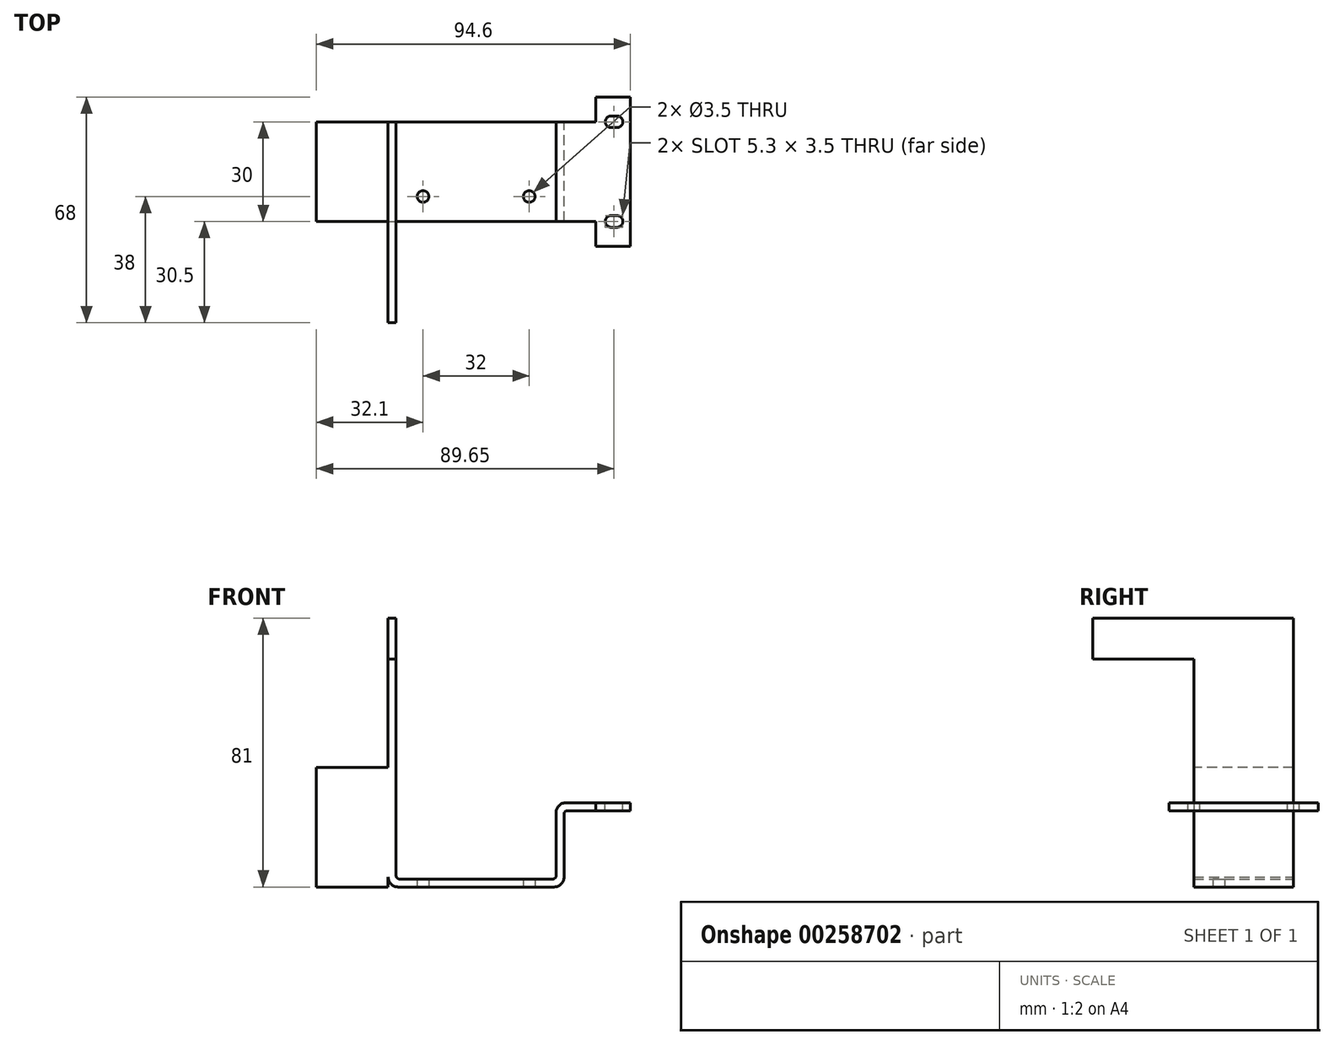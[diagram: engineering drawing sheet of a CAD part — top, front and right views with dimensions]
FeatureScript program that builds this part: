
annotation { "Feature Type Name" : "Feature", "Feature Type Description" : "" }
export const myFeature = defineFeature(function(context is Context, id is Id, definition is map)
    precondition{}
    {
        {
            var Q0;
            Q0=qCreatedBy(makeId("Front.planeOp"),FACE);
            var sketch = newSketch(context, id + "F0", { "sketchPlane" : qUnion([Q0])});
            skLineSegment(sketch, "E0", {"start": v(0, 0) * mm, "end": v(-53, 0) * mm});
            skLineSegment(sketch, "E1", {"start": v(-53, 0) * mm, "end": v(-53, 81) * mm});
            skLineSegment(sketch, "E2", {"start": v(-53, 81) * mm, "end": v(-50.6, 81) * mm});
            skLineSegment(sketch, "E3", {"start": v(-50.6, 81) * mm, "end": v(-50.6, 2.4) * mm});
            skLineSegment(sketch, "E4", {"start": v(-50.6, 2.4) * mm, "end": v(-2.4, 2.4) * mm});
            skLineSegment(sketch, "E5", {"start": v(-2.4, 2.4) * mm, "end": v(-2.4, 25.4) * mm});
            skLineSegment(sketch, "E6", {"start": v(-2.4, 25.4) * mm, "end": v(20, 25.4) * mm});
            skLineSegment(sketch, "E7", {"start": v(20, 25.4) * mm, "end": v(20, 23) * mm});
            skLineSegment(sketch, "E8", {"start": v(20, 23) * mm, "end": v(0, 23) * mm});
            skLineSegment(sketch, "E9", {"start": v(0, 23) * mm, "end": v(0, 0) * mm});
            skSolve(sketch);
        }
        {
            var Q0;
            Q0=makeQuery(id+"F0.imprint","IMPRINT",FACE,{"disambiguationData":[TD([[makeQuery(id+"F0.imprint","IMPRINT",EDGE,{"derivedFrom":sQuery(id+"F0.wireOp",EDGE,"E0")}),-1.0]])]});
            extrude(context, id + "F1", {"entities" : qUnion([Q0]), "endBound" : BoundingType.SYMMETRIC, "depth" : 30 * mm});
        }
        {
            var Q0;
            Q0=makeQuery(id+"F1.opExtrude","CAP_FACE",FACE,{"disambiguationData":[OSD([sQuery(id+"F0.wireOp",EDGE,"E0"),sQuery(id+"F0.wireOp",EDGE,"E1"),sQuery(id+"F0.wireOp",EDGE,"E2"),sQuery(id+"F0.wireOp",EDGE,"E3"),sQuery(id+"F0.wireOp",EDGE,"E4"),sQuery(id+"F0.wireOp",EDGE,"E5"),sQuery(id+"F0.wireOp",EDGE,"E6"),sQuery(id+"F0.wireOp",EDGE,"E7"),sQuery(id+"F0.wireOp",EDGE,"E8"),sQuery(id+"F0.wireOp",EDGE,"E9")])],"isStart":false});
            var sketch = newSketch(context, id + "F2", { "sketchPlane" : qUnion([Q0])});
            skLineSegment(sketch, "E10", {"start": v(-53, 68.7) * mm, "end": v(-50.6, 68.7) * mm});
            skLineSegment(sketch, "E11", {"start": v(9.5, 25.4) * mm, "end": v(9.5, 23) * mm});
            skSolve(sketch);
        }
        {
            var Q0;
            {var subQ0=sQuery(id+"F2.wireOp",EDGE,"E10");Q0=makeQuery(id+"F2.imprint","IMPRINT",FACE,{"disambiguationData":[TD([[makeQuery(id+"F2.imprint","IMPRINT",EDGE,{"derivedFrom":subQ0}),1.0]])]});}
            extrude(context, id + "F3", {"entities" : qUnion([Q0]), "operationType" : NewBodyOperationType.ADD, "depth" : 30.5 * mm});
        }
        {
            var Q0;
            {var subQ0=sQuery(id+"F2.wireOp",EDGE,"E11");Q0=makeQuery(id+"F2.imprint","IMPRINT",FACE,{"disambiguationData":[TD([[makeQuery(id+"F2.imprint","IMPRINT",EDGE,{"derivedFrom":subQ0}),1.0]])]});}
            extrude(context, id + "F4", {"entities" : qUnion([Q0]), "operationType" : NewBodyOperationType.ADD, "depth" : 7.5 * mm});
        }
        {
            var Q0;
            Q0=makeQuery(id+"F1.opExtrude","CAP_FACE",FACE,{"disambiguationData":[OSD([sQuery(id+"F0.wireOp",EDGE,"E0"),sQuery(id+"F0.wireOp",EDGE,"E1"),sQuery(id+"F0.wireOp",EDGE,"E2"),sQuery(id+"F0.wireOp",EDGE,"E3"),sQuery(id+"F0.wireOp",EDGE,"E4"),sQuery(id+"F0.wireOp",EDGE,"E5"),sQuery(id+"F0.wireOp",EDGE,"E6"),sQuery(id+"F0.wireOp",EDGE,"E7"),sQuery(id+"F0.wireOp",EDGE,"E8"),sQuery(id+"F0.wireOp",EDGE,"E9")])],"isStart":true});
            var sketch = newSketch(context, id + "F5", { "sketchPlane" : qUnion([Q0])});
            skLineSegment(sketch, "E12", {"start": v(-9.5, 25.4) * mm, "end": v(-9.5, 23) * mm});
            skSolve(sketch);
        }
        {
            var Q0;
            {var subQ0=sQuery(id+"F5.wireOp",EDGE,"E12");Q0=makeQuery(id+"F5.imprint","IMPRINT",FACE,{"disambiguationData":[TD([[makeQuery(id+"F5.imprint","IMPRINT",EDGE,{"derivedFrom":subQ0}),-1.0]])]});}
            extrude(context, id + "F6", {"entities" : qUnion([Q0]), "operationType" : NewBodyOperationType.ADD, "depth" : 7.5 * mm});
        }
        {
            var Q0;
            {var subQ0=sQuery(id+"F0.wireOp",EDGE,"E6");Q0=makeQuery(id+"F6.boolean.opBoolean","MERGE",FACE,{"derivedFrom":[makeQuery(id+"F4.boolean.opBoolean","MERGE",FACE,{"derivedFrom":[makeQuery(id+"F1.opExtrude","SWEPT_FACE",FACE,{"disambiguationData":[OSD([subQ0])]}),makeQuery(id+"F4.opExtrude","SWEPT_FACE",FACE,{"disambiguationData":[OSD([subQ0])]})]}),makeQuery(id+"F6.opExtrude","SWEPT_FACE",FACE,{"disambiguationData":[OSD([subQ0])]})]});}
            var sketch = newSketch(context, id + "F7", { "sketchPlane" : qUnion([Q0])});
            skCircle(sketch, "E13", {"center": v(14.15, 15) * mm, "radius": 1.75 * mm});
            skCircle(sketch, "E14", {"center": v(15.95, 15) * mm, "radius": 1.75 * mm});
            skCircle(sketch, "E15", {"center": v(14.15, -15) * mm, "radius": 1.75 * mm});
            skCircle(sketch, "E16", {"center": v(15.95, -15) * mm, "radius": 1.75 * mm});
            skLineSegment(sketch, "E17", {"start": v(20, 0) * mm, "end": v(0, 0) * mm, "construction": true});
            skLineSegment(sketch, "E18", {"start": v(14.15, 16.75) * mm, "end": v(15.95, 16.75) * mm});
            skLineSegment(sketch, "E19", {"start": v(15.95, 13.25) * mm, "end": v(14.15, 13.25) * mm});
            skLineSegment(sketch, "E20", {"start": v(14.15, -13.25) * mm, "end": v(15.95, -13.25) * mm});
            skLineSegment(sketch, "E21", {"start": v(14.15, -16.75) * mm, "end": v(15.95, -16.75) * mm});
            skSolve(sketch);
        }
        {
            var Q0;
            {var subQ0=sQuery(id+"F7.wireOp",EDGE,"E15");var subQ1=makeQuery(id+"F7.imprint","INTERSECT",VERTEX,{"derivedFrom":[subQ0,sQuery(id+"F7.wireOp",EDGE,"E20")]});Q0=makeQuery(id+"F7.imprint","IMPRINT",FACE,{"disambiguationData":[TD([[makeQuery(id+"F7.imprint","IMPRINT",EDGE,{"disambiguationData":[TD([[subQ1,1.0]])],"derivedFrom":subQ0}),1.0]])]});}
            var Q1;
            {var subQ0=sQuery(id+"F7.wireOp",EDGE,"E16");var subQ1=sQuery(id+"F7.wireOp",EDGE,"E15");var subQ2=makeQuery(id+"F7.imprint","INTERSECT",VERTEX,{"disambiguationData":[OD(0.0)],"derivedFrom":[subQ1,subQ0]});Q1=makeQuery(id+"F7.imprint","IMPRINT",FACE,{"disambiguationData":[TD([[makeQuery(id+"F7.imprint","IMPRINT",EDGE,{"disambiguationData":[TD([[subQ2,1.0]])],"derivedFrom":subQ1}),1.0]])]});}
            var Q2;
            {var subQ0=sQuery(id+"F7.wireOp",EDGE,"E16");var subQ1=sQuery(id+"F7.wireOp",EDGE,"E15");var subQ2=makeQuery(id+"F7.imprint","INTERSECT",VERTEX,{"disambiguationData":[OD(0.0)],"derivedFrom":[subQ1,subQ0]});Q2=makeQuery(id+"F7.imprint","IMPRINT",FACE,{"disambiguationData":[TD([[makeQuery(id+"F7.imprint","IMPRINT",EDGE,{"disambiguationData":[TD([[subQ2,1.0]])],"derivedFrom":subQ1}),-1.0]])]});}
            var Q3;
            {var subQ0=sQuery(id+"F7.wireOp",EDGE,"E20");Q3=makeQuery(id+"F7.imprint","IMPRINT",FACE,{"disambiguationData":[TD([[makeQuery(id+"F7.imprint","IMPRINT",EDGE,{"derivedFrom":subQ0}),-1.0]])]});}
            var Q4;
            {var subQ0=sQuery(id+"F7.wireOp",EDGE,"E21");Q4=makeQuery(id+"F7.imprint","IMPRINT",FACE,{"disambiguationData":[TD([[makeQuery(id+"F7.imprint","IMPRINT",EDGE,{"derivedFrom":subQ0}),1.0]])]});}
            var Q5;
            {var subQ0=sQuery(id+"F7.wireOp",EDGE,"E13");var subQ1=makeQuery(id+"F7.imprint","INTERSECT",VERTEX,{"derivedFrom":[subQ0,sQuery(id+"F7.wireOp",EDGE,"E18")]});Q5=makeQuery(id+"F7.imprint","IMPRINT",FACE,{"disambiguationData":[TD([[makeQuery(id+"F7.imprint","IMPRINT",EDGE,{"disambiguationData":[TD([[subQ1,1.0]])],"derivedFrom":subQ0}),1.0]])]});}
            var Q6;
            {var subQ0=sQuery(id+"F7.wireOp",EDGE,"E14");var subQ1=sQuery(id+"F7.wireOp",EDGE,"E13");var subQ2=makeQuery(id+"F7.imprint","INTERSECT",VERTEX,{"disambiguationData":[OD(0.0)],"derivedFrom":[subQ1,subQ0]});Q6=makeQuery(id+"F7.imprint","IMPRINT",FACE,{"disambiguationData":[TD([[makeQuery(id+"F7.imprint","IMPRINT",EDGE,{"disambiguationData":[TD([[subQ2,1.0]])],"derivedFrom":subQ1}),1.0]])]});}
            var Q7;
            {var subQ0=sQuery(id+"F7.wireOp",EDGE,"E14");var subQ1=sQuery(id+"F7.wireOp",EDGE,"E13");var subQ2=makeQuery(id+"F7.imprint","INTERSECT",VERTEX,{"disambiguationData":[OD(0.0)],"derivedFrom":[subQ1,subQ0]});Q7=makeQuery(id+"F7.imprint","IMPRINT",FACE,{"disambiguationData":[TD([[makeQuery(id+"F7.imprint","IMPRINT",EDGE,{"disambiguationData":[TD([[subQ2,1.0]])],"derivedFrom":subQ1}),-1.0]])]});}
            var Q8;
            {var subQ0=sQuery(id+"F7.wireOp",EDGE,"E18");Q8=makeQuery(id+"F7.imprint","IMPRINT",FACE,{"disambiguationData":[TD([[makeQuery(id+"F7.imprint","IMPRINT",EDGE,{"derivedFrom":subQ0}),-1.0]])]});}
            var Q9;
            {var subQ0=sQuery(id+"F7.wireOp",EDGE,"E19");Q9=makeQuery(id+"F7.imprint","IMPRINT",FACE,{"disambiguationData":[TD([[makeQuery(id+"F7.imprint","IMPRINT",EDGE,{"derivedFrom":subQ0}),-1.0]])]});}
            var Q10;
            {var subQ0=sQuery(id+"F0.wireOp",EDGE,"E8");Q10=makeQuery(id+"F6.boolean.opBoolean","MERGE",FACE,{"derivedFrom":[makeQuery(id+"F4.boolean.opBoolean","MERGE",FACE,{"derivedFrom":[makeQuery(id+"F1.opExtrude","SWEPT_FACE",FACE,{"disambiguationData":[OSD([subQ0])]}),makeQuery(id+"F4.opExtrude","SWEPT_FACE",FACE,{"disambiguationData":[OSD([subQ0])]})]}),makeQuery(id+"F6.opExtrude","SWEPT_FACE",FACE,{"disambiguationData":[OSD([subQ0])]})]});}
            extrude(context, id + "F8", {"entities" : qUnion([Q0, Q1, Q2, Q3, Q4, Q5, Q6, Q7, Q8, Q9]), "operationType" : NewBodyOperationType.REMOVE, "endBound" : BoundingType.UP_TO_SURFACE, "oppositeDirection" : true, "endBoundEntityFace" : qUnion([Q10]), "depth" : 25 * mm});
        }
        {
            var Q0;
            Q0=makeQuery(id+"F1.opExtrude","SWEPT_EDGE",EDGE,{"disambiguationData":[OSD([sQuery(id+"F0.wireOp",EDGE,"E5"),sQuery(id+"F0.wireOp",EDGE,"E6")])]});
            var Q1;
            Q1=makeQuery(id+"F1.opExtrude","SWEPT_EDGE",EDGE,{"disambiguationData":[OSD([sQuery(id+"F0.wireOp",EDGE,"E0"),sQuery(id+"F0.wireOp",EDGE,"E9")])]});
            var Q2;
            Q2=makeQuery(id+"F1.opExtrude","SWEPT_EDGE",EDGE,{"disambiguationData":[OSD([sQuery(id+"F0.wireOp",EDGE,"E0"),sQuery(id+"F0.wireOp",EDGE,"E1")])]});
            fillet(context, id + "F9", {"entities" : qUnion([Q0, Q1, Q2]), "radius" : 3 * mm, "tangentPropagation" : true, "allowEdgeOverflow" : false});
        }
        {
            var Q0;
            Q0=makeQuery(id+"F1.opExtrude","SWEPT_EDGE",EDGE,{"disambiguationData":[OSD([sQuery(id+"F0.wireOp",EDGE,"E3"),sQuery(id+"F0.wireOp",EDGE,"E4")])]});
            var Q1;
            Q1=makeQuery(id+"F1.opExtrude","SWEPT_EDGE",EDGE,{"disambiguationData":[OSD([sQuery(id+"F0.wireOp",EDGE,"E4"),sQuery(id+"F0.wireOp",EDGE,"E5")])]});
            var Q2;
            Q2=makeQuery(id+"F1.opExtrude","SWEPT_EDGE",EDGE,{"disambiguationData":[OSD([sQuery(id+"F0.wireOp",EDGE,"E8"),sQuery(id+"F0.wireOp",EDGE,"E9")])]});
            fillet(context, id + "F10", {"entities" : qUnion([Q0, Q1, Q2]), "radius" : 1 * mm, "tangentPropagation" : true, "allowEdgeOverflow" : false});
        }
        {
            var Q0;
            {var subQ0=sQuery(id+"F0.wireOp",EDGE,"E1");Q0=makeQuery(id+"F3.boolean.opBoolean","MERGE",FACE,{"derivedFrom":[makeQuery(id+"F1.opExtrude","SWEPT_FACE",FACE,{"disambiguationData":[OSD([subQ0])]}),makeQuery(id+"F3.opExtrude","SWEPT_FACE",FACE,{"disambiguationData":[OSD([subQ0])]})]});}
            var sketch = newSketch(context, id + "F11", { "sketchPlane" : qUnion([Q0])});
            skLineSegment(sketch, "E22.bottom", {"start": v(-15, 36) * mm, "end": v(15, 36) * mm});
            skLineSegment(sketch, "E22.top", {"start": v(-15, 0) * mm, "end": v(15, 0) * mm});
            skLineSegment(sketch, "E22.left", {"start": v(-15, 36) * mm, "end": v(-15, 0) * mm});
            skLineSegment(sketch, "E22.right", {"start": v(15, 36) * mm, "end": v(15, 0) * mm});
            skSolve(sketch);
        }
        {
            var Q0;
            {var subQ0=sQuery(id+"F11.wireOp",EDGE,"E22.bottom");Q0=makeQuery(id+"F11.imprint","IMPRINT",FACE,{"disambiguationData":[TD([[makeQuery(id+"F11.imprint","IMPRINT",EDGE,{"derivedFrom":subQ0}),-1.0]])]});}
            var Q1;
            {var subQ0=sQuery(id+"F11.wireOp",EDGE,"E22.top");Q1=makeQuery(id+"F11.imprint","IMPRINT",FACE,{"disambiguationData":[TD([[makeQuery(id+"F11.imprint","IMPRINT",EDGE,{"derivedFrom":subQ0}),1.0]])]});}
            extrude(context, id + "F12", {"entities" : qUnion([Q0, Q1]), "operationType" : NewBodyOperationType.ADD, "depth" : 21.6 * mm});
        }
        {
            var Q0;
            Q0=makeQuery(id+"F1.opExtrude","SWEPT_FACE",FACE,{"disambiguationData":[OSD([sQuery(id+"F0.wireOp",EDGE,"E0")])]});
            var sketch = newSketch(context, id + "F13", { "sketchPlane" : qUnion([Q0])});
            skCircle(sketch, "E23", {"center": v(-42.5, 7.5) * mm, "radius": 1.75 * mm});
            skCircle(sketch, "E24", {"center": v(-10.5, 7.5) * mm, "radius": 1.75 * mm});
            skLineSegment(sketch, "E25", {"start": v(-26.5, -18.57) * mm, "end": v(-26.5, 24.2) * mm, "construction": true});
            skPoint(sketch, "E25.startSnap0", {"position": v(-26.5, -15) * mm});
            skSolve(sketch);
        }
        {
            var Q0;
            Q0=makeQuery(id+"F13.imprint","IMPRINT",FACE,{"disambiguationData":[TD([[makeQuery(id+"F13.imprint","IMPRINT",EDGE,{"derivedFrom":sQuery(id+"F13.wireOp",EDGE,"E23")}),1.0]])]});
            var Q1;
            Q1=makeQuery(id+"F13.imprint","IMPRINT",FACE,{"disambiguationData":[TD([[makeQuery(id+"F13.imprint","IMPRINT",EDGE,{"derivedFrom":sQuery(id+"F13.wireOp",EDGE,"E24")}),1.0]])]});
            var Q2;
            Q2=makeQuery(id+"F1.opExtrude","SWEPT_FACE",FACE,{"disambiguationData":[OSD([sQuery(id+"F0.wireOp",EDGE,"E4")])]});
            extrude(context, id + "F14", {"entities" : qUnion([Q0, Q1]), "operationType" : NewBodyOperationType.REMOVE, "endBound" : BoundingType.UP_TO_SURFACE, "oppositeDirection" : true, "endBoundEntityFace" : qUnion([Q2]), "depth" : 25 * mm});
        }
    });
